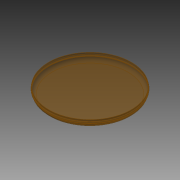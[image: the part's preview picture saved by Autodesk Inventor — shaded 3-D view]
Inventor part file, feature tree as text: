
AUTODESK INVENTOR PART (.ipt)
format: ipt  version: 2014 (Build 180170000, 170)  size: 164,864 bytes
history: native  units: in
note: dims shown in document units (in); Inventor stores cm internally (conversion verified against a paired STEP export)
features: reference x2, revolve x1, sketch x1
ambient origin geometry x8: Origin, YZ Plane, XZ Plane, XY Plane, X Axis, Y Axis, Z Axis, Center Point
bodies: Solid1 (feature_tree)
feature tree (4):
  revolve  "Revolution1"  [1 undecoded]
  sketch  "Sketch1"  dims[d0=0.025in d1=0.002in d2=90.0deg]
  reference  "Reference1"
  reference  "Reference2"
note: 1 required parameter value undecoded (feature->parameter linkage not recoverable at this tier; creation-order binding heuristic only, values carry confidence <= 0.55)
